# Revit family: NARROW 2216 IP 20_S242240.N.1
name_source: partatom
category: Luminarias
units: mm (PartAtom-declared; Revit-internal decimal feet)

## family parameters
Compartido = No
Corte con vacíos al cargar = No
Cota de conector redondo = Diámetro de uso
Origen de luz = Sí
Punto de cálculo de habitación = No
Se basa en plano de trabajo = Sí
Siempre vertical = No
Tipo de pieza = Normal

## types (1)
- NARROW 2216 IP 20_S242240.N.1
    Ancho = 6 mm  [stored 0.019685 ft]
    Archivo de red fotométrica = S242240.N.1 IES.IES
    Cambio de temperatura de color de luz atenuada = <Ninguno>
    Comentarios de vataje = 24V
    Costo = 0 $
    Descripción = TIRA LED NARROW 6MM DE ANCHO IP20 USO PARA INTERIORES, DE PCB BLANCO SIN RECUBRIMIENTO, MONO CROMATICA, CON UNA POTENCIA DE 19.2W/M DE UN TIPO DE LED 2216 SMD, IRC90, 240 LEDS POR METRO, PRESENTACION DE 5M, TEMPERATURA EN BLANCO FRIO 4000K, 1670 LUMENES POR METRO, EFICIENCIA DE 87 LM/W, CORTE A 2.5CM, ALIMENTADA A 24V, REQUIERE ACCESORIOS COMO FUENTE DE PODER Y CABLE DE ALIMENTACION. PERFIL EN CASO DE SER NECESARIO.
    Elevación por defecto = 0 mm  [stored 0 ft]
    Fabricante = BRILLANT
    Filtro de color = 16777215
    Longitud de línea de emisión = 600 mm  [stored 1.9685 ft]
    Lámpara = 2216 SMD
    Modelo = S242240.N.1
    Ángulo de inclinación = 60.00°

note: [stored X ft] marks values corroborated as IEEE doubles in the binary element streams (Revit-internal decimal feet)

## geometry (parser evidence)
native form markers: Blend x2
no freeform markers — native parametric forms only
